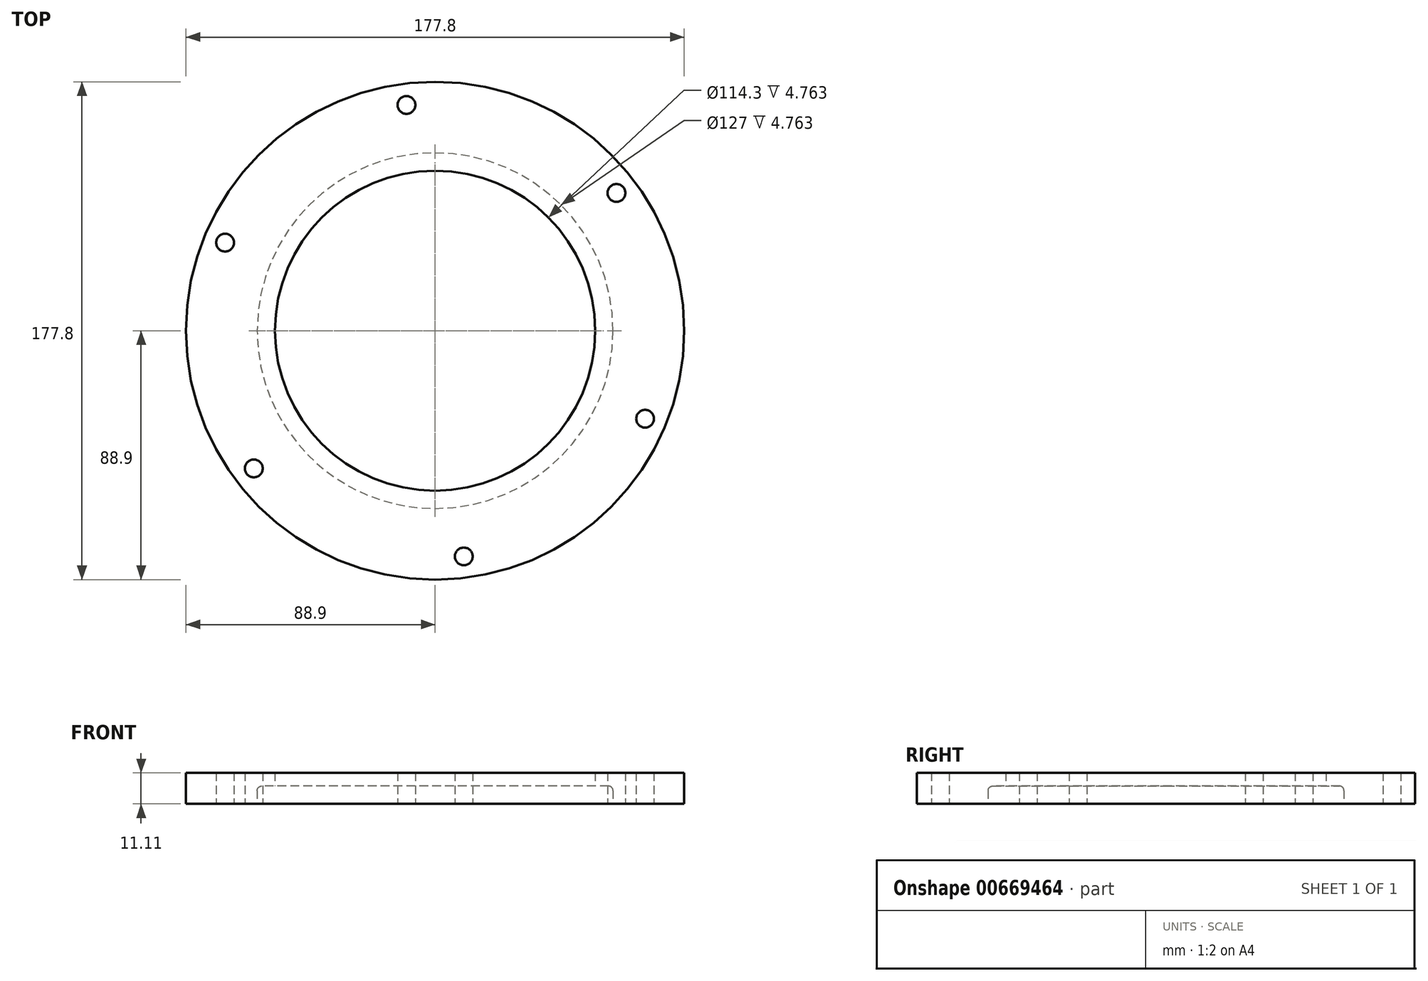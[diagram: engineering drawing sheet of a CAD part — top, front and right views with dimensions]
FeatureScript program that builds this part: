
annotation { "Feature Type Name" : "Feature", "Feature Type Description" : "" }
export const myFeature = defineFeature(function(context is Context, id is Id, definition is map)
    precondition{}
    {
        {
            var Q0;
            Q0=qCreatedBy(makeId("Top.planeOp"),FACE);
            var sketch = newSketch(context, id + "F0", { "sketchPlane" : qUnion([Q0])});
            skCircle(sketch, "E0", {"center": v(0, 0) * mm, "radius": 88.9 * mm});
            skCircle(sketch, "E1", {"center": v(0, 0) * mm, "radius": 57.15 * mm});
            skSolve(sketch);
        }
        {
            var Q0;
            Q0=makeQuery(id+"F0.imprint","IMPRINT",FACE,{"disambiguationData":[TD([[makeQuery(id+"F0.imprint","IMPRINT",EDGE,{"derivedFrom":sQuery(id+"F0.wireOp",EDGE,"E0")}),1.0]])]});
            extrude(context, id + "F1", {"entities" : qUnion([Q0]), "depth" : 11.1 * mm, "offsetDistance" : 25.4 * mm});
        }
        {
            var Q0;
            Q0=qCreatedBy(makeId("Top.planeOp"),FACE);
            var sketch = newSketch(context, id + "F2", { "sketchPlane" : qUnion([Q0])});
            skCircle(sketch, "E2", {"center": v(0, 0) * mm, "radius": 63.5 * mm});
            skSolve(sketch);
        }
        {
            var Q0;
            Q0=makeQuery(id+"F2.imprint","IMPRINT",FACE,{"disambiguationData":[TD([[makeQuery(id+"F2.imprint","IMPRINT",EDGE,{"derivedFrom":sQuery(id+"F2.wireOp",EDGE,"E2")}),1.0]])]});
            extrude(context, id + "F3", {"entities" : qUnion([Q0]), "operationType" : NewBodyOperationType.REMOVE, "depth" : 6.35 * mm, "offsetDistance" : 25.4 * mm});
        }
        {
            var Q0;
            Q0=qCreatedBy(makeId("Top.planeOp"),FACE);
            var sketch = newSketch(context, id + "F4", { "sketchPlane" : qUnion([Q0])});
            skCircle(sketch, "E3", {"center": v(-74.95, 31.45) * mm, "radius": 4.82 * mm});
            skCircle(sketch, "E4.1.0", {"center": v(-64.7, -49.18) * mm, "radius": 4.82 * mm});
            skCircle(sketch, "E4.2.0", {"center": v(10.24, -80.63) * mm, "radius": 4.82 * mm});
            skCircle(sketch, "E4.3.0", {"center": v(74.95, -31.45) * mm, "radius": 4.82 * mm});
            skCircle(sketch, "E4.4.0", {"center": v(64.7, 49.18) * mm, "radius": 4.82 * mm});
            skCircle(sketch, "E4.5.0", {"center": v(-10.24, 80.63) * mm, "radius": 4.82 * mm});
            skPoint(sketch, "E4.center", {"position": v(0, 0) * mm});
            skSolve(sketch);
        }
        {
            var Q0;
            Q0=sQuery(id+"F4.wireOp",VERTEX,"E4.2.0.center");
            var Q1;
            Q1=sQuery(id+"F4.wireOp",VERTEX,"E4.1.0.center");
            var Q2;
            Q2=sQuery(id+"F4.wireOp",VERTEX,"E3.center");
            var Q3;
            Q3=sQuery(id+"F4.wireOp",VERTEX,"E4.5.0.center");
            var Q4;
            Q4=sQuery(id+"F4.wireOp",VERTEX,"E4.4.0.center");
            var Q5;
            Q5=sQuery(id+"F4.wireOp",VERTEX,"E4.3.0.center");
            var Q6;
            Q6=makeQuery(id+"F1.opExtrude","SWEPT_BODY",BODY,{"disambiguationData":[OSD([sQuery(id+"F0.wireOp",EDGE,"E0"),sQuery(id+"F0.wireOp",EDGE,"E1")])]});
            hole(context, id + "F5", {"style" : HoleStyle.SIMPLE, "endStyle" : HoleEndStyle.THROUGH, "oppositeDirection" : true, "holeDiameter" : 6.35 * mm, "majorDiameter" : 6.35 * mm, "isTappedThrough" : true, "tappedDepth" : 12.7 * mm, "tapClearance" : 3, "locations" : qUnion([Q0, Q1, Q2, Q3, Q4, Q5]), "scope" : qUnion([Q6])});
        }
        {
            var Q0;
            Q0=makeQuery(id+"F3.boolean.opBoolean","COPY",EDGE,{"derivedFrom":makeQuery(id+"F3.opExtrude","CAP_EDGE",EDGE,{"disambiguationData":[OSD([sQuery(id+"F2.wireOp",EDGE,"E2")])],"isStart":false})});
            fillet(context, id + "F6", {"entities" : qUnion([Q0]), "radius" : 1.59 * mm, "tangentPropagation" : true, "allowEdgeOverflow" : false});
        }
    });
